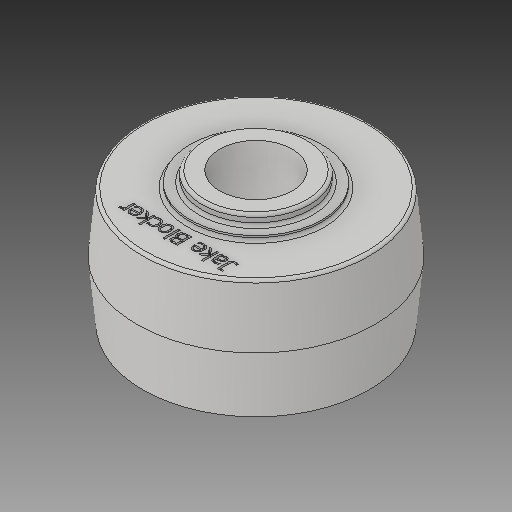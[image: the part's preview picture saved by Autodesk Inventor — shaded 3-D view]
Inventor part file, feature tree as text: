
AUTODESK INVENTOR PART (.ipt)
format: ipt  version: 2019 (Build 230136000, 136)  size: 465,408 bytes
history: native  units: in
note: dims shown in document units (in); Inventor stores cm internally (conversion verified against a paired STEP export)
features: fillet x4, sketch x3, revolve x1, extrude x1, emboss x1
ambient origin geometry x8: Origin, YZ Plane, XZ Plane, XY Plane, X Axis, Y Axis, Z Axis, Center Point
bodies: Solid1 (feature_tree)
feature tree (10):
  revolve  "Revolution1"  [1 undecoded]
  fillet  "Fillet1"  Radius=0.072in
  fillet  "Fillet2"  Radius=0.08in
  fillet  "Fillet3"  Radius=0.032in
  fillet  "Fillet4"  Radius=0.78in
  extrude  "Extrusion1"  TaperAngle=90.0deg  [1 undecoded]
  emboss  "Emboss1"
  sketch  "Sketch1"  dims[d0=0.3721in d1=0.513in d2=0.072in d3=0.08in d4=0.032in d5=0.78in]
  sketch  "Sketch2"  dims[d6=0.819in d7=90.0deg]
  sketch  "Sketch3"  dims[d8=0.02in d9=0.02in d10=0.02in d11=0.02in d12=0.5in d13=2.0in d14=0.0in d15=0.1in d16=0.0in]
note: 2 required parameter values undecoded (feature->parameter linkage not recoverable at this tier; creation-order binding heuristic only, values carry confidence <= 0.55)